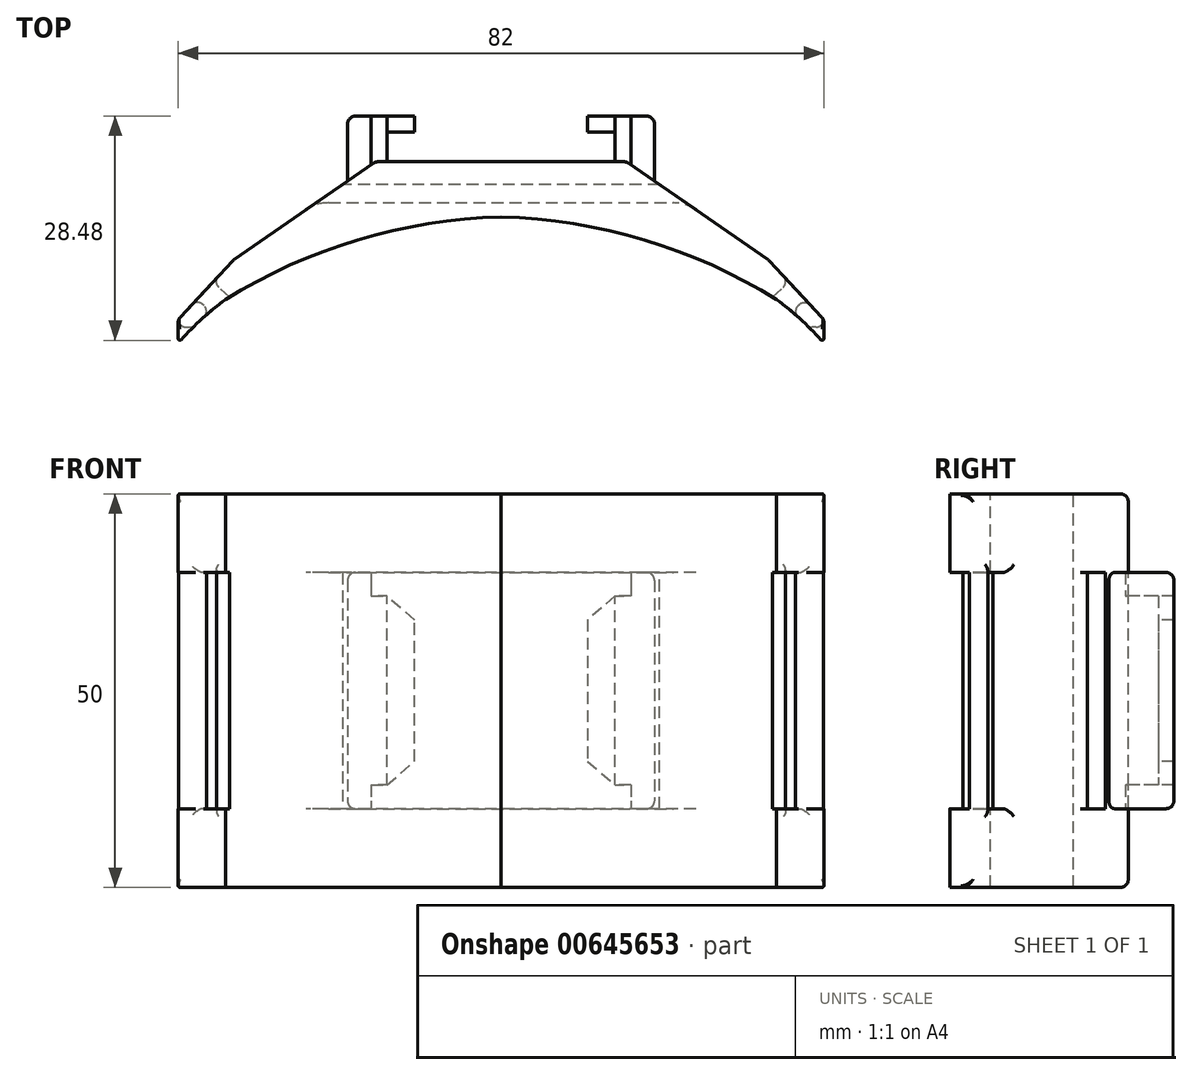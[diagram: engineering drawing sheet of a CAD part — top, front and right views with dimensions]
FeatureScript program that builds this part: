
annotation { "Feature Type Name" : "Feature", "Feature Type Description" : "" }
export const myFeature = defineFeature(function(context is Context, id is Id, definition is map)
    precondition{}
    {
        {
            var Q0;
            Q0=qCreatedBy(makeId("Top.planeOp"),FACE);
            var sketch = newSketch(context, id + "F0", { "sketchPlane" : qUnion([Q0])});
            skArc(sketch, "E0", {"start": v(0, 0) * mm, "mid": v(-18.2, -2.93) * mm, "end": v(-35, -10.5) * mm});
            skArc(sketch, "E1", {"start": v(-35, -10.5) * mm, "mid": v(-38.14, -13.1) * mm, "end": v(-41, -16) * mm});
            skLineSegment(sketch, "E2", {"start": v(-41, -16) * mm, "end": v(-41, -13) * mm});
            skLineSegment(sketch, "E3", {"start": v(0, 7) * mm, "end": v(-15.94, 7) * mm});
            skLineSegment(sketch, "E4", {"start": v(0, 0) * mm, "end": v(0, 7) * mm});
            skLineSegment(sketch, "E5", {"start": v(-41, -13) * mm, "end": v(-34, -5.5) * mm});
            skLineSegment(sketch, "E6", {"start": v(-34, -5.5) * mm, "end": v(-15.94, 7) * mm});
            skPoint(sketch, "E7", {"position": v(-41, -13) * mm});
            skSolve(sketch);
        }
        {
            var Q0;
            Q0 = qSketchRegion(id + "F0", true);
            extrude(context, id + "F1", {"entities" : qUnion([Q0]), "oppositeDirection" : true, "depth" : 50 * mm, "offsetDistance" : 25 * mm});
        }
        {
            var Q0;
            Q0=makeQuery(id+"F1.opExtrude","SWEPT_FACE",FACE,{"disambiguationData":[OSD([sQuery(id+"F0.wireOp",EDGE,"E5")])]});
            var sketch = newSketch(context, id + "F2", { "sketchPlane" : qUnion([Q0])});
            skLineSegment(sketch, "E8.bottom", {"start": v(31, -40) * mm, "end": v(34, -40) * mm});
            skLineSegment(sketch, "E8.top", {"start": v(31, -10) * mm, "end": v(34, -10) * mm});
            skLineSegment(sketch, "E8.left", {"start": v(34, -40) * mm, "end": v(34, -10) * mm});
            skLineSegment(sketch, "E8.right", {"start": v(31, -40) * mm, "end": v(31, -10) * mm});
            skSolve(sketch);
        }
        {
            var Q0;
            Q0 = qSketchRegion(id + "F2", true);
            extrude(context, id + "F3", {"entities" : qUnion([Q0]), "operationType" : NewBodyOperationType.REMOVE, "oppositeDirection" : true, "depth" : 25 * mm, "offsetDistance" : 25 * mm});
        }
        {
            var Q0;
            Q0=qCreatedBy(makeId("Right.planeOp"),FACE);
            var sketch = newSketch(context, id + "F4", { "sketchPlane" : qUnion([Q0])});
            skLineSegment(sketch, "E9.bottom", {"start": v(-17, -40) * mm, "end": v(-14, -40) * mm});
            skLineSegment(sketch, "E9.top", {"start": v(-17, -10) * mm, "end": v(-14, -10) * mm});
            skLineSegment(sketch, "E9.left", {"start": v(-17, -40) * mm, "end": v(-17, -10) * mm});
            skLineSegment(sketch, "E9.right", {"start": v(-14, -40) * mm, "end": v(-14, -10) * mm});
            skSolve(sketch);
        }
        {
            var Q0;
            Q0 = qSketchRegion(id + "F4", true);
            extrude(context, id + "F5", {"entities" : qUnion([Q0]), "operationType" : NewBodyOperationType.REMOVE, "oppositeDirection" : true, "depth" : 205 * mm, "offsetDistance" : 25 * mm});
        }
        {
            var Q0;
            Q0=makeQuery(id+"F1.opExtrude","SWEPT_FACE",FACE,{"disambiguationData":[OSD([sQuery(id+"F0.wireOp",EDGE,"E6")])]});
            fillet(context, id + "F6", {"entities" : qUnion([Q0]), "radius" : 1 * mm, "tangentPropagation" : true, "allowEdgeOverflow" : false});
        }
        {
            var Q0;
            Q0=makeQuery(id+"F1.opExtrude","SWEPT_FACE",FACE,{"disambiguationData":[OSD([sQuery(id+"F0.wireOp",EDGE,"E5")])]});
            fillet(context, id + "F7", {"entities" : qUnion([Q0]), "radius" : 1 * mm, "tangentPropagation" : true, "allowEdgeOverflow" : false});
        }
        {
            var Q0;
            {var subQ0=sQuery(id+"F0.wireOp",EDGE,"E2");var subQ1=sQuery(id+"F0.wireOp",EDGE,"E1");Q0=makeQuery(id+"F5.boolean.opBoolean","SPLIT",EDGE,{"disambiguationData":[TD([makeQuery(id+"F5.opExtrude","SWEPT_FACE",FACE,{"disambiguationData":[OSD([sQuery(id+"F4.wireOp",EDGE,"E9.bottom")])]})])],"derivedFrom":makeQuery(id+"F1.opExtrude","SWEPT_EDGE",EDGE,{"disambiguationData":[OSD([subQ1,subQ0])]})});}
            var Q1;
            {var subQ0=sQuery(id+"F0.wireOp",EDGE,"E2");var subQ1=sQuery(id+"F0.wireOp",EDGE,"E1");Q1=makeQuery(id+"F5.boolean.opBoolean","SPLIT",EDGE,{"disambiguationData":[TD([makeQuery(id+"F5.opExtrude","SWEPT_FACE",FACE,{"disambiguationData":[OSD([sQuery(id+"F4.wireOp",EDGE,"E9.top")])]})])],"derivedFrom":makeQuery(id+"F1.opExtrude","SWEPT_EDGE",EDGE,{"disambiguationData":[OSD([subQ1,subQ0])]})});}
            var Q2;
            Q2=makeQuery(id+"F1.opExtrude","CAP_EDGE",EDGE,{"disambiguationData":[OSD([sQuery(id+"F0.wireOp",EDGE,"E2")])],"isStart":false});
            var Q3;
            Q3=makeQuery(id+"F7.opFillet","BLEND_EDGE",EDGE,{"blendedFrom":[makeQuery(id+"F1.opExtrude","CAP_EDGE",EDGE,{"disambiguationData":[OSD([sQuery(id+"F0.wireOp",EDGE,"E5")])],"isStart":false}),makeQuery(id+"F1.opExtrude","SWEPT_FACE",FACE,{"disambiguationData":[OSD([sQuery(id+"F0.wireOp",EDGE,"E2")])]})],"blendedInto":[makeQuery(id+"F1.opExtrude","SWEPT_FACE",FACE,{"disambiguationData":[OSD([sQuery(id+"F0.wireOp",EDGE,"E2")])]})]});
            var Q4;
            Q4=makeQuery(id+"F1.opExtrude","CAP_EDGE",EDGE,{"disambiguationData":[OSD([sQuery(id+"F0.wireOp",EDGE,"E2")])],"isStart":true});
            var Q5;
            Q5=makeQuery(id+"F7.opFillet","BLEND_EDGE",EDGE,{"blendedFrom":[makeQuery(id+"F1.opExtrude","CAP_EDGE",EDGE,{"disambiguationData":[OSD([sQuery(id+"F0.wireOp",EDGE,"E5")])],"isStart":true}),makeQuery(id+"F1.opExtrude","SWEPT_FACE",FACE,{"disambiguationData":[OSD([sQuery(id+"F0.wireOp",EDGE,"E2")])]})],"blendedInto":[makeQuery(id+"F1.opExtrude","SWEPT_FACE",FACE,{"disambiguationData":[OSD([sQuery(id+"F0.wireOp",EDGE,"E2")])]})]});
            fillet(context, id + "F8", {"entities" : qUnion([Q0, Q1, Q2, Q3, Q4, Q5]), "radius" : 0.2 * mm, "tangentPropagation" : true, "allowEdgeOverflow" : false});
        }
        {
            var Q0;
            Q0=makeQuery(id+"F3.boolean.opBoolean","INTERSECT",EDGE,{"derivedFrom":[makeQuery(id+"F1.opExtrude","SWEPT_FACE",FACE,{"disambiguationData":[OSD([sQuery(id+"F0.wireOp",EDGE,"E1")])]}),makeQuery(id+"F3.opExtrude","SWEPT_FACE",FACE,{"disambiguationData":[OSD([sQuery(id+"F2.wireOp",EDGE,"E8.left")])]})]});
            var Q1;
            Q1=makeQuery(id+"F5.boolean.opBoolean","INTERSECT",EDGE,{"derivedFrom":[makeQuery(id+"F1.opExtrude","SWEPT_FACE",FACE,{"disambiguationData":[OSD([sQuery(id+"F0.wireOp",EDGE,"E1")])]}),makeQuery(id+"F5.opExtrude","SWEPT_FACE",FACE,{"disambiguationData":[OSD([sQuery(id+"F4.wireOp",EDGE,"E9.right")])]})]});
            var Q2;
            Q2=makeQuery(id+"F5.boolean.opBoolean","INTERSECT",EDGE,{"derivedFrom":[makeQuery(id+"F1.opExtrude","SWEPT_FACE",FACE,{"disambiguationData":[OSD([sQuery(id+"F0.wireOp",EDGE,"E2")])]}),makeQuery(id+"F5.opExtrude","SWEPT_FACE",FACE,{"disambiguationData":[OSD([sQuery(id+"F4.wireOp",EDGE,"E9.right")])]})]});
            fillet(context, id + "F9", {"entities" : qUnion([Q0, Q1, Q2]), "radius" : 1 * mm, "tangentPropagation" : true, "allowEdgeOverflow" : false});
        }
        {
            var Q0;
            Q0=makeQuery(id+"F1.opExtrude","SWEPT_BODY",BODY,{"disambiguationData":[OSD([sQuery(id+"F0.wireOp",EDGE,"E0"),sQuery(id+"F0.wireOp",EDGE,"E1"),sQuery(id+"F0.wireOp",EDGE,"E2"),sQuery(id+"F0.wireOp",EDGE,"E3"),sQuery(id+"F0.wireOp",EDGE,"E4"),sQuery(id+"F0.wireOp",EDGE,"E5"),sQuery(id+"F0.wireOp",EDGE,"E6")])]});
            var Q1;
            Q1=qCreatedBy(makeId("Right.planeOp"),FACE);
            mirror(context, id + "F10", {"operationType" : NewBodyOperationType.ADD, "entities" : qUnion([Q0]), "mirrorPlane" : qUnion([Q1])});
        }
        {
            var Q0;
            {var subQ0=makeQuery(id+"F1.opExtrude","SWEPT_FACE",FACE,{"disambiguationData":[OSD([sQuery(id+"F0.wireOp",EDGE,"E3")])]});Q0=makeQuery(id+"F10.boolean.opBoolean","MERGE",FACE,{"derivedFrom":[subQ0,makeQuery(id+"F10.opPattern","COPY",FACE,{"derivedFrom":subQ0,"instanceName":"1"})]});}
            fillet(context, id + "F11", {"entities" : qUnion([Q0]), "radius" : 1 * mm, "tangentPropagation" : true, "allowEdgeOverflow" : false});
        }
        {
            var Q0;
            {var subQ0=makeQuery(id+"F1.opExtrude","SWEPT_FACE",FACE,{"disambiguationData":[OSD([sQuery(id+"F0.wireOp",EDGE,"E3")])]});Q0=makeQuery(id+"F10.boolean.opBoolean","MERGE",FACE,{"derivedFrom":[subQ0,makeQuery(id+"F10.opPattern","COPY",FACE,{"derivedFrom":subQ0,"instanceName":"1"})]});}
            var sketch = newSketch(context, id + "F12", { "sketchPlane" : qUnion([Q0])});
            skLineSegment(sketch, "E10.bottom", {"start": v(-19.5, -10) * mm, "end": v(-16.5, -10) * mm});
            skLineSegment(sketch, "E10.top", {"start": v(-19.5, -40) * mm, "end": v(-16.5, -40) * mm});
            skLineSegment(sketch, "E10.left", {"start": v(-19.5, -10) * mm, "end": v(-19.5, -40) * mm});
            skLineSegment(sketch, "E10.right", {"start": v(-16.5, -10) * mm, "end": v(-16.5, -13) * mm});
            skLineSegment(sketch, "E11.bottom", {"start": v(-16.5, -13) * mm, "end": v(-14.5, -13) * mm});
            skLineSegment(sketch, "E11.top", {"start": v(-16.5, -37) * mm, "end": v(-14.5, -37) * mm});
            skLineSegment(sketch, "E11.right", {"start": v(-14.5, -13) * mm, "end": v(-14.5, -37) * mm});
            skLineSegment(sketch, "E12.bottom", {"start": v(19.5, -10) * mm, "end": v(16.5, -10) * mm});
            skLineSegment(sketch, "E12.top", {"start": v(19.5, -40) * mm, "end": v(16.5, -40) * mm});
            skLineSegment(sketch, "E12.left", {"start": v(19.5, -10) * mm, "end": v(19.5, -40) * mm});
            skLineSegment(sketch, "E12.right", {"start": v(16.5, -10) * mm, "end": v(16.5, -13) * mm});
            skLineSegment(sketch, "E13.bottom", {"start": v(16.5, -13) * mm, "end": v(14.5, -13) * mm});
            skLineSegment(sketch, "E13.top", {"start": v(16.5, -37) * mm, "end": v(14.5, -37) * mm});
            skLineSegment(sketch, "E13.right", {"start": v(14.5, -13) * mm, "end": v(14.5, -37) * mm});
            skLineSegment(sketch, "E14.trimOffspring", {"start": v(-16.5, -37) * mm, "end": v(-16.5, -40) * mm});
            skLineSegment(sketch, "E15.trimOffspring", {"start": v(16.5, -37) * mm, "end": v(16.5, -40) * mm});
            skSolve(sketch);
        }
        {
            var Q0;
            Q0 = qSketchRegion(id + "F12", true);
            extrude(context, id + "F13", {"entities" : qUnion([Q0]), "operationType" : NewBodyOperationType.ADD, "depth" : 3.8 * mm, "offsetDistance" : 25 * mm, "hasSecondDirection" : true, "secondDirectionOppositeDirection" : true, "secondDirectionDepth" : 3 * mm});
        }
        {
            var Q0;
            Q0=makeQuery(id+"F13.opExtrude","CAP_FACE",FACE,{"disambiguationData":[OSD([sQuery(id+"F12.wireOp",EDGE,"E10.bottom"),sQuery(id+"F12.wireOp",EDGE,"E10.top"),sQuery(id+"F12.wireOp",EDGE,"E10.left"),sQuery(id+"F12.wireOp",EDGE,"E10.right"),sQuery(id+"F12.wireOp",EDGE,"E11.bottom"),sQuery(id+"F12.wireOp",EDGE,"E11.top"),sQuery(id+"F12.wireOp",EDGE,"E11.right"),sQuery(id+"F12.wireOp",EDGE,"E14.trimOffspring")])],"isStart":false});
            var sketch = newSketch(context, id + "F14", { "sketchPlane" : qUnion([Q0])});
            skLineSegment(sketch, "E16", {"start": v(-16.5, -40) * mm, "end": v(-19.5, -40) * mm});
            skLineSegment(sketch, "E17", {"start": v(-19.5, -40) * mm, "end": v(-19.5, -10) * mm});
            skLineSegment(sketch, "E18", {"start": v(-19.5, -10) * mm, "end": v(-16.5, -10) * mm});
            skLineSegment(sketch, "E19", {"start": v(-16.5, -10) * mm, "end": v(-16.5, -13) * mm});
            skLineSegment(sketch, "E20", {"start": v(-16.5, -13) * mm, "end": v(-14.5, -13) * mm});
            skLineSegment(sketch, "E21", {"start": v(-14.5, -13) * mm, "end": v(-11, -16) * mm});
            skLineSegment(sketch, "E22", {"start": v(-11, -16) * mm, "end": v(-11, -34) * mm});
            skLineSegment(sketch, "E23", {"start": v(-11, -34) * mm, "end": v(-14.5, -37) * mm});
            skLineSegment(sketch, "E24", {"start": v(-14.5, -37) * mm, "end": v(-16.5, -37) * mm});
            skLineSegment(sketch, "E25", {"start": v(-16.5, -37) * mm, "end": v(-16.5, -40) * mm});
            skSolve(sketch);
        }
        {
            var Q0;
            Q0 = qSketchRegion(id + "F14", true);
            extrude(context, id + "F15", {"entities" : qUnion([Q0]), "operationType" : NewBodyOperationType.ADD, "depth" : 2 * mm, "offsetDistance" : 25 * mm});
        }
        {
            var Q0;
            Q0=makeQuery(id+"F13.opExtrude","CAP_FACE",FACE,{"disambiguationData":[OSD([sQuery(id+"F12.wireOp",EDGE,"E12.bottom"),sQuery(id+"F12.wireOp",EDGE,"E12.top"),sQuery(id+"F12.wireOp",EDGE,"E12.left"),sQuery(id+"F12.wireOp",EDGE,"E12.right"),sQuery(id+"F12.wireOp",EDGE,"E13.bottom"),sQuery(id+"F12.wireOp",EDGE,"E13.top"),sQuery(id+"F12.wireOp",EDGE,"E13.right"),sQuery(id+"F12.wireOp",EDGE,"E15.trimOffspring")])],"isStart":false});
            var sketch = newSketch(context, id + "F16", { "sketchPlane" : qUnion([Q0])});
            skLineSegment(sketch, "E26", {"start": v(16.5, -13) * mm, "end": v(16.5, -10) * mm});
            skLineSegment(sketch, "E27", {"start": v(16.5, -10) * mm, "end": v(19.5, -10) * mm});
            skLineSegment(sketch, "E28", {"start": v(19.5, -10) * mm, "end": v(19.5, -40) * mm});
            skLineSegment(sketch, "E29", {"start": v(19.5, -40) * mm, "end": v(16.5, -40) * mm});
            skLineSegment(sketch, "E30", {"start": v(16.5, -40) * mm, "end": v(16.5, -37) * mm});
            skLineSegment(sketch, "E31", {"start": v(16.5, -37) * mm, "end": v(14.5, -37) * mm});
            skLineSegment(sketch, "E32", {"start": v(14.5, -37) * mm, "end": v(11, -34) * mm});
            skLineSegment(sketch, "E33", {"start": v(11, -34) * mm, "end": v(11, -16) * mm});
            skLineSegment(sketch, "E34", {"start": v(11, -16) * mm, "end": v(14.5, -13) * mm});
            skLineSegment(sketch, "E35", {"start": v(14.5, -13) * mm, "end": v(16.5, -13) * mm});
            skSolve(sketch);
        }
        {
            var Q0;
            Q0 = qSketchRegion(id + "F16", true);
            extrude(context, id + "F17", {"entities" : qUnion([Q0]), "operationType" : NewBodyOperationType.ADD, "depth" : 2 * mm, "offsetDistance" : 25 * mm});
        }
        {
            var Q0;
            Q0=makeQuery(id+"F17.boolean.opBoolean","MERGE",EDGE,{"derivedFrom":[makeQuery(id+"F13.opExtrude","SWEPT_EDGE",EDGE,{"disambiguationData":[OSD([sQuery(id+"F12.wireOp",EDGE,"E12.top"),sQuery(id+"F12.wireOp",EDGE,"E12.left")])]}),makeQuery(id+"F17.opExtrude","SWEPT_EDGE",EDGE,{"disambiguationData":[OSD([sQuery(id+"F16.wireOp",EDGE,"E28"),sQuery(id+"F16.wireOp",EDGE,"E29")])]})]});
            var Q1;
            Q1=makeQuery(id+"F17.opExtrude","CAP_EDGE",EDGE,{"disambiguationData":[OSD([sQuery(id+"F16.wireOp",EDGE,"E28")])],"isStart":false});
            var Q2;
            Q2=makeQuery(id+"F17.boolean.opBoolean","MERGE",EDGE,{"derivedFrom":[makeQuery(id+"F13.opExtrude","SWEPT_EDGE",EDGE,{"disambiguationData":[OSD([sQuery(id+"F12.wireOp",EDGE,"E12.bottom"),sQuery(id+"F12.wireOp",EDGE,"E12.left")])]}),makeQuery(id+"F17.opExtrude","SWEPT_EDGE",EDGE,{"disambiguationData":[OSD([sQuery(id+"F16.wireOp",EDGE,"E27"),sQuery(id+"F16.wireOp",EDGE,"E28")])]})]});
            var Q3;
            Q3=makeQuery(id+"F17.opExtrude","CAP_EDGE",EDGE,{"disambiguationData":[OSD([sQuery(id+"F16.wireOp",EDGE,"E29")])],"isStart":false});
            var Q4;
            Q4=makeQuery(id+"F17.opExtrude","CAP_EDGE",EDGE,{"disambiguationData":[OSD([sQuery(id+"F16.wireOp",EDGE,"E27")])],"isStart":false});
            var Q5;
            Q5=makeQuery(id+"F15.opExtrude","CAP_EDGE",EDGE,{"disambiguationData":[OSD([sQuery(id+"F14.wireOp",EDGE,"E18")])],"isStart":false});
            var Q6;
            Q6=makeQuery(id+"F15.boolean.opBoolean","MERGE",EDGE,{"derivedFrom":[makeQuery(id+"F13.opExtrude","SWEPT_EDGE",EDGE,{"disambiguationData":[OSD([sQuery(id+"F12.wireOp",EDGE,"E10.bottom"),sQuery(id+"F12.wireOp",EDGE,"E10.left")])]}),makeQuery(id+"F15.opExtrude","SWEPT_EDGE",EDGE,{"disambiguationData":[OSD([sQuery(id+"F14.wireOp",EDGE,"E17"),sQuery(id+"F14.wireOp",EDGE,"E18")])]})]});
            var Q7;
            Q7=makeQuery(id+"F15.opExtrude","CAP_EDGE",EDGE,{"disambiguationData":[OSD([sQuery(id+"F14.wireOp",EDGE,"E17")])],"isStart":false});
            var Q8;
            Q8=makeQuery(id+"F15.opExtrude","CAP_EDGE",EDGE,{"disambiguationData":[OSD([sQuery(id+"F14.wireOp",EDGE,"E16")])],"isStart":false});
            var Q9;
            Q9=makeQuery(id+"F15.boolean.opBoolean","MERGE",EDGE,{"derivedFrom":[makeQuery(id+"F13.opExtrude","SWEPT_EDGE",EDGE,{"disambiguationData":[OSD([sQuery(id+"F12.wireOp",EDGE,"E10.top"),sQuery(id+"F12.wireOp",EDGE,"E10.left")])]}),makeQuery(id+"F15.opExtrude","SWEPT_EDGE",EDGE,{"disambiguationData":[OSD([sQuery(id+"F14.wireOp",EDGE,"E16"),sQuery(id+"F14.wireOp",EDGE,"E17")])]})]});
            fillet(context, id + "F18", {"entities" : qUnion([Q0, Q1, Q2, Q3, Q4, Q5, Q6, Q7, Q8, Q9]), "radius" : 1 * mm, "tangentPropagation" : true, "allowEdgeOverflow" : false});
        }
        {
            var Q0;
            Q0=makeQuery(id+"F10.opPattern","COPY",FACE,{"derivedFrom":makeQuery(id+"F3.boolean.opBoolean","COPY",FACE,{"derivedFrom":makeQuery(id+"F3.opExtrude","SWEPT_FACE",FACE,{"disambiguationData":[OSD([sQuery(id+"F2.wireOp",EDGE,"E8.bottom")])]})}),"instanceName":"1"});
            var sketch = newSketch(context, id + "F19", { "sketchPlane" : qUnion([Q0])});
            skLineSegment(sketch, "E36", {"start": v(22.18, 4.09) * mm, "end": v(-22.28, 4.09) * mm});
            skLineSegment(sketch, "E37", {"start": v(-22.28, 4.09) * mm, "end": v(-25.53, 1.79) * mm});
            skLineSegment(sketch, "E38", {"start": v(-25.53, 1.79) * mm, "end": v(25.99, 1.79) * mm});
            skLineSegment(sketch, "E39", {"start": v(25.99, 1.79) * mm, "end": v(22.18, 4.09) * mm});
            skSolve(sketch);
        }
        {
            var Q0;
            Q0 = qSketchRegion(id + "F19", true);
            extrude(context, id + "F20", {"entities" : qUnion([Q0]), "operationType" : NewBodyOperationType.REMOVE, "depth" : 30 * mm, "offsetDistance" : 25 * mm});
        }
        {
            var Q0;
            Q0=makeQuery(id+"F20.boolean.opBoolean","INTERSECT",EDGE,{"derivedFrom":[makeQuery(id+"F1.opExtrude","SWEPT_FACE",FACE,{"disambiguationData":[OSD([sQuery(id+"F0.wireOp",EDGE,"E6")])]}),makeQuery(id+"F20.opExtrude","SWEPT_FACE",FACE,{"disambiguationData":[OSD([sQuery(id+"F19.wireOp",EDGE,"E38")])]})]});
            var Q1;
            Q1=makeQuery(id+"F20.boolean.opBoolean","INTERSECT",EDGE,{"derivedFrom":[makeQuery(id+"F10.opPattern","COPY",FACE,{"derivedFrom":makeQuery(id+"F1.opExtrude","SWEPT_FACE",FACE,{"disambiguationData":[OSD([sQuery(id+"F0.wireOp",EDGE,"E6")])]}),"instanceName":"1"}),makeQuery(id+"F20.opExtrude","SWEPT_FACE",FACE,{"disambiguationData":[OSD([sQuery(id+"F19.wireOp",EDGE,"E38")])]})]});
            fillet(context, id + "F21", {"entities" : qUnion([Q0, Q1]), "radius" : 5 * mm, "tangentPropagation" : true, "allowEdgeOverflow" : false});
        }
    });
